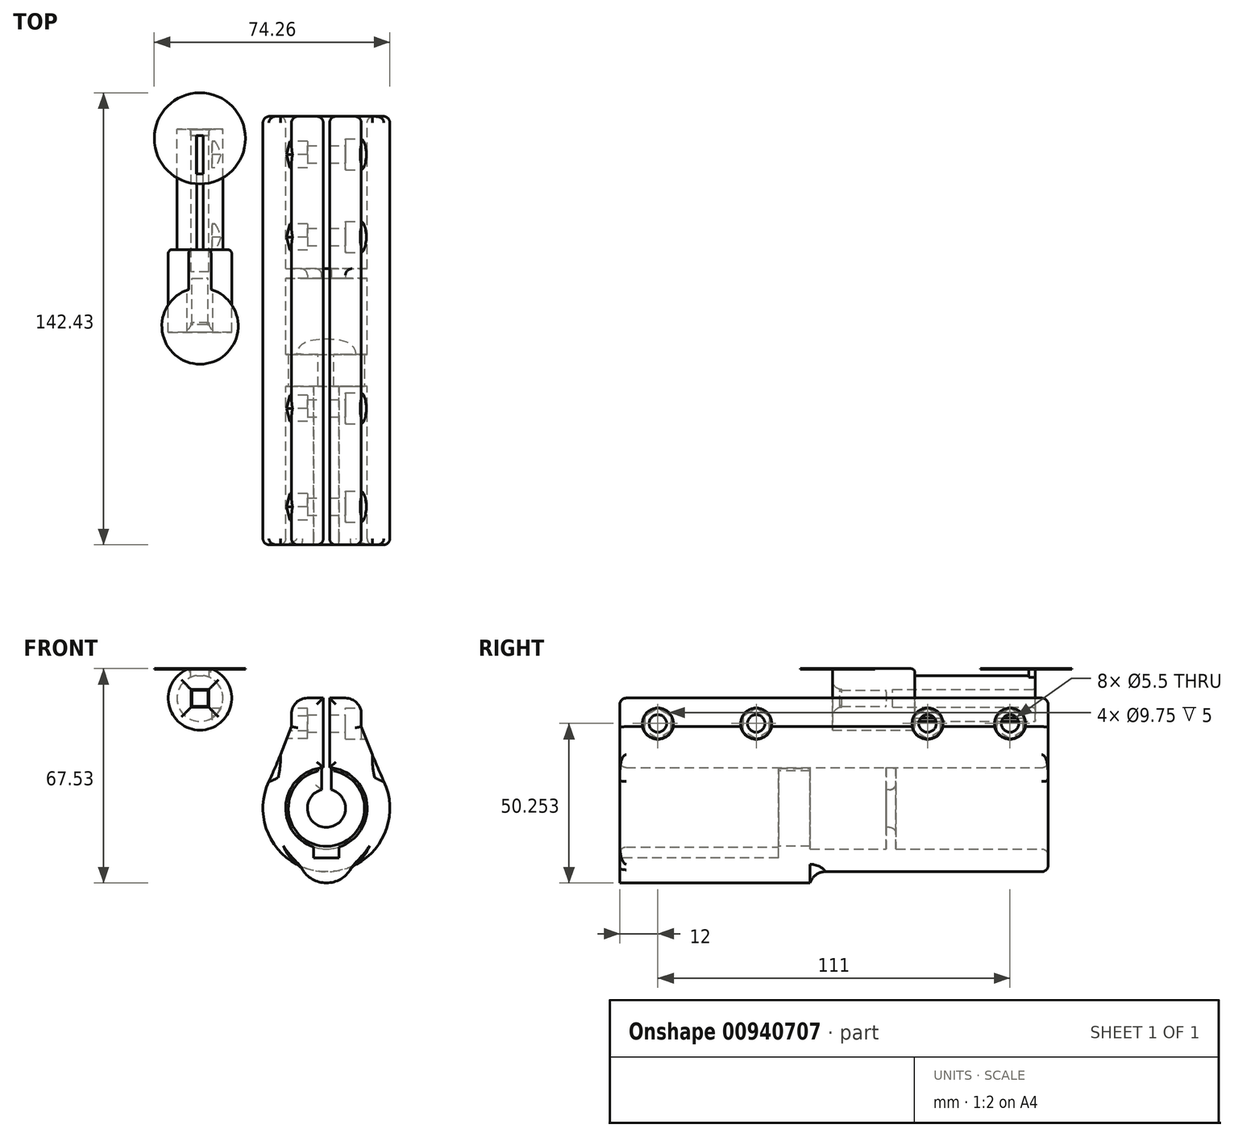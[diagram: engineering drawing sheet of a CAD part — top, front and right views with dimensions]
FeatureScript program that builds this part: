
annotation { "Feature Type Name" : "Feature", "Feature Type Description" : "" }
export const myFeature = defineFeature(function(context is Context, id is Id, definition is map)
    precondition{}
    {
        {
            var Q0;
            Q0=qCreatedBy(makeId("Front.planeOp"),FACE);
            var sketch = newSketch(context, id + "F0", { "sketchPlane" : qUnion([Q0])});
            skArc(sketch, "E0", {"start": v(-40.86, 41.8) * mm, "mid": v(-39.86, 27.36) * mm, "end": v(-38.86, 41.8) * mm});
            skLineSegment(sketch, "E1.bottom", {"start": v(-37.05, 31.8) * mm, "end": v(-42.67, 31.8) * mm});
            skLineSegment(sketch, "E1.top", {"start": v(-37.05, 37.42) * mm, "end": v(-42.67, 37.42) * mm});
            skLineSegment(sketch, "E1.left", {"start": v(-37.05, 31.8) * mm, "end": v(-37.05, 37.42) * mm});
            skLineSegment(sketch, "E1.right", {"start": v(-42.67, 31.8) * mm, "end": v(-42.67, 37.42) * mm});
            skLineSegment(sketch, "E2", {"start": v(-40.86, 41.8) * mm, "end": v(-38.86, 41.8) * mm});
            skArc(sketch, "E3", {"start": v(-43.36, 43.98) * mm, "mid": v(-39.86, 24.61) * mm, "end": v(-36.36, 43.98) * mm});
            skLineSegment(sketch, "E4", {"start": v(-43.36, 43.98) * mm, "end": v(-36.36, 43.98) * mm});
            skLineSegment(sketch, "E5.bottom", {"start": v(-37.76, 32.11) * mm, "end": v(-41.96, 32.11) * mm});
            skLineSegment(sketch, "E5.top", {"start": v(-37.76, 37.11) * mm, "end": v(-41.96, 37.11) * mm});
            skLineSegment(sketch, "E5.left", {"start": v(-37.36, 32.51) * mm, "end": v(-37.36, 36.71) * mm});
            skLineSegment(sketch, "E5.right", {"start": v(-42.36, 32.51) * mm, "end": v(-42.36, 36.71) * mm});
            skPoint(sketch, "E6.visualSharp", {"position": v(-42.36, 37.11) * mm});
            skArc(sketch, "E6.filletArc", {"start": v(-41.96, 37.11) * mm, "mid": v(-42.24, 37) * mm, "end": v(-42.36, 36.71) * mm});
            skPoint(sketch, "E7.visualSharp", {"position": v(-37.36, 37.11) * mm});
            skArc(sketch, "E7.filletArc", {"start": v(-37.36, 36.71) * mm, "mid": v(-37.48, 37) * mm, "end": v(-37.76, 37.11) * mm});
            skPoint(sketch, "E8.visualSharp", {"position": v(-37.36, 32.11) * mm});
            skArc(sketch, "E8.filletArc", {"start": v(-37.76, 32.11) * mm, "mid": v(-37.48, 32.23) * mm, "end": v(-37.36, 32.51) * mm});
            skPoint(sketch, "E9.visualSharp", {"position": v(-42.36, 32.11) * mm});
            skArc(sketch, "E9.filletArc", {"start": v(-42.36, 32.51) * mm, "mid": v(-42.24, 32.23) * mm, "end": v(-41.96, 32.11) * mm});
            skSolve(sketch);
        }
        {
            var Q0;
            Q0=makeQuery(id+"F0.imprint","IMPRINT",FACE,{"disambiguationData":[TD([[makeQuery(id+"F0.imprint","IMPRINT",EDGE,{"derivedFrom":sQuery(id+"F0.wireOp",EDGE,"E0")}),1.0]])]});
            extrude(context, id + "F1", {"entities" : qUnion([Q0]), "depth" : 18 * mm, "offsetDistance" : 25 * mm, "hasSecondDirection" : true, "secondDirectionOppositeDirection" : true, "secondDirectionDepth" : 46 * mm});
        }
        {
            var Q0;
            Q0=makeQuery(id+"F0.imprint","IMPRINT",FACE,{"disambiguationData":[TD([[makeQuery(id+"F0.imprint","IMPRINT",EDGE,{"derivedFrom":sQuery(id+"F0.wireOp",EDGE,"E1.bottom")}),-1.0]])]});
            var Q1;
            Q1=makeQuery(id+"F0.imprint","IMPRINT",FACE,{"disambiguationData":[TD([[makeQuery(id+"F0.imprint","IMPRINT",EDGE,{"derivedFrom":sQuery(id+"F0.wireOp",EDGE,"E5.bottom")}),-1.0]])]});
            extrude(context, id + "F2", {"entities" : qUnion([Q0, Q1]), "depth" : 1 * mm, "offsetDistance" : 25 * mm, "hasSecondDirection" : true, "secondDirectionOppositeDirection" : true, "secondDirectionDepth" : 1 * mm});
        }
        {
            var Q0;
            Q0=makeQuery(id+"F1.opExtrude","CAP_EDGE",EDGE,{"disambiguationData":[OSD([sQuery(id+"F0.wireOp",EDGE,"E1.left")])],"isStart":true});
            var Q1;
            Q1=makeQuery(id+"F1.opExtrude","CAP_EDGE",EDGE,{"disambiguationData":[OSD([sQuery(id+"F0.wireOp",EDGE,"E1.top")])],"isStart":true});
            var Q2;
            Q2=makeQuery(id+"F1.opExtrude","CAP_EDGE",EDGE,{"disambiguationData":[OSD([sQuery(id+"F0.wireOp",EDGE,"E1.right")])],"isStart":true});
            var Q3;
            Q3=makeQuery(id+"F1.opExtrude","CAP_EDGE",EDGE,{"disambiguationData":[OSD([sQuery(id+"F0.wireOp",EDGE,"E1.bottom")])],"isStart":true});
            fillet(context, id + "F3", {"entities" : qUnion([Q0, Q1, Q2, Q3]), "radius" : 1 * mm, "tangentPropagation" : true, "allowEdgeOverflow" : false});
        }
        {
            var Q0;
            Q0=qCreatedBy(makeId("Front.planeOp"),FACE);
            var sketch = newSketch(context, id + "F4", { "sketchPlane" : qUnion([Q0])});
            skLineSegment(sketch, "E10", {"start": v(0, -133.96) * mm, "end": v(0, 109.5) * mm, "construction": true});
            skArc(sketch, "E11", {"start": v(-16.99, 10.56) * mm, "mid": v(0, -20) * mm, "end": v(16.99, 10.56) * mm});
            skArc(sketch, "E12", {"start": v(-1, 12.81) * mm, "mid": v(0, -12.85) * mm, "end": v(1, 12.81) * mm});
            skLineSegment(sketch, "E13.bottom", {"start": v(-11, 34.7) * mm, "end": v(-1, 34.7) * mm});
            skLineSegment(sketch, "E13.left", {"start": v(-11, 34.7) * mm, "end": v(-11, 25.7) * mm});
            skLineSegment(sketch, "E13.right", {"start": v(11, 34.7) * mm, "end": v(11, 25.7) * mm});
            skPoint(sketch, "E13.middle", {"position": v(0, 35.28) * mm});
            skPoint(sketch, "E14.trimOffspring.end.orphan", {"position": v(-11, 35.86) * mm});
            skPoint(sketch, "E15.trimOffspring.end.orphan", {"position": v(11, 35.86) * mm});
            skLineSegment(sketch, "E16.left", {"start": v(-1, 34.7) * mm, "end": v(-1, 12.81) * mm});
            skLineSegment(sketch, "E16.right", {"start": v(1, 34.7) * mm, "end": v(1, 12.81) * mm});
            skPoint(sketch, "E16.middle", {"position": v(0, 52.57) * mm});
            skPoint(sketch, "E17.orphan", {"position": v(1, 29.17) * mm});
            skPoint(sketch, "E16.top.start.orphan", {"position": v(-1, 29.19) * mm});
            skLineSegment(sketch, "E18.trimOffspring", {"start": v(1, 34.7) * mm, "end": v(11, 34.7) * mm});
            skPoint(sketch, "E19.orphan", {"position": v(-1, 75.98) * mm});
            skPoint(sketch, "E20.orphan", {"position": v(1, 75.96) * mm});
            skLineSegment(sketch, "E21", {"start": v(11, 25.7) * mm, "end": v(16.99, 10.56) * mm});
            skLineSegment(sketch, "E22.MirrorCS", {"start": v(-11, 25.7) * mm, "end": v(-16.99, 10.56) * mm});
            skPoint(sketch, "E23.orphan", {"position": v(11, 16.7) * mm});
            skSolve(sketch);
        }
        {
            var Q0;
            Q0=makeQuery(id+"F4.imprint","IMPRINT",FACE,{"disambiguationData":[TD([[makeQuery(id+"F4.imprint","IMPRINT",EDGE,{"derivedFrom":sQuery(id+"F4.wireOp",EDGE,"E11")}),1.0]])]});
            extrude(context, id + "F5", {"entities" : qUnion([Q0]), "depth" : 85 * mm, "offsetDistance" : 25 * mm, "hasSecondDirection" : true, "secondDirectionOppositeDirection" : true, "secondDirectionDepth" : 50 * mm});
        }
        {
            var Q0;
            Q0=makeQuery(id+"F5.opExtrude","CAP_EDGE",EDGE,{"disambiguationData":[OSD([sQuery(id+"F4.wireOp",EDGE,"E12")])],"isStart":true});
            var Q1;
            Q1=makeQuery(id+"F5.opExtrude","CAP_EDGE",EDGE,{"disambiguationData":[OSD([sQuery(id+"F4.wireOp",EDGE,"E12")])],"isStart":false});
            var Q2;
            Q2=makeQuery(id+"F5.opExtrude","CAP_EDGE",EDGE,{"disambiguationData":[OSD([sQuery(id+"F4.wireOp",EDGE,"E11")])],"isStart":true});
            var Q3;
            Q3=makeQuery(id+"F5.opExtrude","CAP_FACE",FACE,{"disambiguationData":[OSD([sQuery(id+"F4.wireOp",EDGE,"E11"),sQuery(id+"F4.wireOp",EDGE,"E12"),sQuery(id+"F4.wireOp",EDGE,"E13.bottom"),sQuery(id+"F4.wireOp",EDGE,"E13.left"),sQuery(id+"F4.wireOp",EDGE,"E13.right"),sQuery(id+"F4.wireOp",EDGE,"E16.left"),sQuery(id+"F4.wireOp",EDGE,"E16.right"),sQuery(id+"F4.wireOp",EDGE,"E18.trimOffspring")])],"isStart":true});
            var Q4;
            Q4=makeQuery(id+"F5.opExtrude","CAP_FACE",FACE,{"disambiguationData":[OSD([sQuery(id+"F4.wireOp",EDGE,"E11"),sQuery(id+"F4.wireOp",EDGE,"E12"),sQuery(id+"F4.wireOp",EDGE,"E13.bottom"),sQuery(id+"F4.wireOp",EDGE,"E13.left"),sQuery(id+"F4.wireOp",EDGE,"E13.right"),sQuery(id+"F4.wireOp",EDGE,"E16.left"),sQuery(id+"F4.wireOp",EDGE,"E16.right"),sQuery(id+"F4.wireOp",EDGE,"E18.trimOffspring")])],"isStart":false});
            fillet(context, id + "F6", {"entities" : qUnion([Q0, Q1, Q2, Q3, Q4]), "radius" : 2 * mm, "tangentPropagation" : true, "allowEdgeOverflow" : false});
        }
        {
            var Q0;
            Q0=makeQuery(id+"F5.opExtrude","SWEPT_FACE",FACE,{"disambiguationData":[OSD([sQuery(id+"F4.wireOp",EDGE,"E13.right")])]});
            var sketch = newSketch(context, id + "F7", { "sketchPlane" : qUnion([Q0])});
            skLineSegment(sketch, "E24", {"start": v(-11, 26.7) * mm, "end": v(-81, 26.7) * mm, "construction": true});
            skPoint(sketch, "E25", {"position": v(38, 26.7) * mm});
            skPoint(sketch, "E26", {"position": v(12, 26.7) * mm});
            skPoint(sketch, "E27", {"position": v(-42, 26.7) * mm});
            skPoint(sketch, "E28", {"position": v(-73, 26.7) * mm});
            skSolve(sketch);
        }
        {
            var Q0;
            Q0=sQuery(id+"F7.wireOp",VERTEX,"E25");
            var Q1;
            Q1=sQuery(id+"F7.wireOp",VERTEX,"E26");
            var Q2;
            Q2=sQuery(id+"F7.wireOp",VERTEX,"E27");
            var Q3;
            Q3=sQuery(id+"F7.wireOp",VERTEX,"E28");
            var Q4;
            Q4=makeQuery(id+"F1.opExtrude","SWEPT_BODY",BODY,{"disambiguationData":[OSD([sQuery(id+"F0.wireOp",EDGE,"E0"),sQuery(id+"F0.wireOp",EDGE,"E1.bottom"),sQuery(id+"F0.wireOp",EDGE,"E1.top"),sQuery(id+"F0.wireOp",EDGE,"E1.left"),sQuery(id+"F0.wireOp",EDGE,"E1.right")])]});
            var Q5;
            Q5=makeQuery(id+"F5.opExtrude","SWEPT_BODY",BODY,{"disambiguationData":[OSD([sQuery(id+"F4.wireOp",EDGE,"E11"),sQuery(id+"F4.wireOp",EDGE,"E12"),sQuery(id+"F4.wireOp",EDGE,"E13.bottom"),sQuery(id+"F4.wireOp",EDGE,"E13.left"),sQuery(id+"F4.wireOp",EDGE,"E13.right"),sQuery(id+"F4.wireOp",EDGE,"E16.left"),sQuery(id+"F4.wireOp",EDGE,"E16.right"),sQuery(id+"F4.wireOp",EDGE,"E18.trimOffspring")])]});
            hole(context, id + "F8", {"style" : HoleStyle.C_BORE, "endStyle" : HoleEndStyle.BLIND, "standardTappedOrClearance" : lookupTablePath({ "fit" : "Normal", "standard" : "ISO", "size" : "M5", "type" : "Clearance" }), "standardBlindInLast" : lookupTablePath({ "fit" : "Normal", "standard" : "ISO", "engagement" : "75%", "pitch" : "0.8 mm", "size" : "M5", "type" : "Clearance & tapped" }), "holeDiameter" : 5.5 * mm, "cBoreDiameter" : 9.75 * mm, "cBoreDepth" : 5 * mm, "majorDiameter" : 5 * mm, "holeDepth" : 35 * mm, "isTappedThrough" : true, "tappedDepth" : 12 * mm, "tapClearance" : 3, "locations" : qUnion([Q0, Q1, Q2, Q3]), "scope" : qUnion([Q4, Q5])});
        }
        {
            var Q0;
            Q0=makeQuery(id+"F5.opExtrude","SWEPT_FACE",FACE,{"disambiguationData":[OSD([sQuery(id+"F4.wireOp",EDGE,"E13.left")])]});
            var sketch = newSketch(context, id + "F9", { "sketchPlane" : qUnion([Q0])});
            skPoint(sketch, "E29", {"position": v(73, 26.7) * mm});
            skPoint(sketch, "E30", {"position": v(42, 26.7) * mm});
            skPoint(sketch, "E31", {"position": v(-12, 26.7) * mm});
            skPoint(sketch, "E32", {"position": v(-38, 26.7) * mm});
            skCircle(sketch, "E33.cCircle", {"center": v(73, 26.7) * mm, "radius": 4.15 * mm, "construction": true});
            skLineSegment(sketch, "E33.0", {"start": v(77.15, 29.1) * mm, "end": v(77.15, 24.3) * mm});
            skLineSegment(sketch, "E33.1", {"start": v(77.15, 24.3) * mm, "end": v(73, 21.91) * mm});
            skLineSegment(sketch, "E33.2", {"start": v(73, 21.91) * mm, "end": v(68.85, 24.3) * mm});
            skLineSegment(sketch, "E33.3", {"start": v(68.85, 24.3) * mm, "end": v(68.85, 29.1) * mm});
            skLineSegment(sketch, "E33.4", {"start": v(68.85, 29.1) * mm, "end": v(73, 31.5) * mm});
            skLineSegment(sketch, "E33.5", {"start": v(73, 31.5) * mm, "end": v(77.15, 29.1) * mm});
            skPoint(sketch, "E33.0.midPoint", {"position": v(77.15, 26.7) * mm});
            skCircle(sketch, "E34.cCircle", {"center": v(42, 26.7) * mm, "radius": 4.15 * mm, "construction": true});
            skLineSegment(sketch, "E34.0", {"start": v(46.15, 29.1) * mm, "end": v(46.15, 24.3) * mm});
            skLineSegment(sketch, "E34.1", {"start": v(46.15, 24.3) * mm, "end": v(42, 21.91) * mm});
            skLineSegment(sketch, "E34.2", {"start": v(42, 21.91) * mm, "end": v(37.85, 24.3) * mm});
            skLineSegment(sketch, "E34.3", {"start": v(37.85, 24.3) * mm, "end": v(37.85, 29.1) * mm});
            skLineSegment(sketch, "E34.4", {"start": v(37.85, 29.1) * mm, "end": v(42, 31.5) * mm});
            skLineSegment(sketch, "E34.5", {"start": v(42, 31.5) * mm, "end": v(46.15, 29.1) * mm});
            skPoint(sketch, "E34.0.midPoint", {"position": v(46.15, 26.7) * mm});
            skCircle(sketch, "E35.cCircle", {"center": v(-12, 26.7) * mm, "radius": 4.15 * mm, "construction": true});
            skLineSegment(sketch, "E35.0", {"start": v(-7.85, 29.1) * mm, "end": v(-7.85, 24.3) * mm});
            skLineSegment(sketch, "E35.1", {"start": v(-7.85, 24.3) * mm, "end": v(-12, 21.91) * mm});
            skLineSegment(sketch, "E35.2", {"start": v(-12, 21.91) * mm, "end": v(-16.15, 24.3) * mm});
            skLineSegment(sketch, "E35.3", {"start": v(-16.15, 24.3) * mm, "end": v(-16.15, 29.1) * mm});
            skLineSegment(sketch, "E35.4", {"start": v(-16.15, 29.1) * mm, "end": v(-12, 31.5) * mm});
            skLineSegment(sketch, "E35.5", {"start": v(-12, 31.5) * mm, "end": v(-7.85, 29.1) * mm});
            skPoint(sketch, "E35.0.midPoint", {"position": v(-7.85, 26.7) * mm});
            skCircle(sketch, "E36.cCircle", {"center": v(-38, 26.7) * mm, "radius": 4.15 * mm, "construction": true});
            skLineSegment(sketch, "E36.0", {"start": v(-33.85, 29.1) * mm, "end": v(-33.85, 24.3) * mm});
            skLineSegment(sketch, "E36.1", {"start": v(-33.85, 24.3) * mm, "end": v(-38, 21.91) * mm});
            skLineSegment(sketch, "E36.2", {"start": v(-38, 21.91) * mm, "end": v(-42.15, 24.3) * mm});
            skLineSegment(sketch, "E36.3", {"start": v(-42.15, 24.3) * mm, "end": v(-42.15, 29.1) * mm});
            skLineSegment(sketch, "E36.4", {"start": v(-42.15, 29.1) * mm, "end": v(-38, 31.5) * mm});
            skLineSegment(sketch, "E36.5", {"start": v(-38, 31.5) * mm, "end": v(-33.85, 29.1) * mm});
            skPoint(sketch, "E36.0.midPoint", {"position": v(-33.85, 26.7) * mm});
            skSolve(sketch);
        }
        {
            var Q0;
            Q0=qCreatedBy(makeId("Front.planeOp"),FACE);
            var sketch = newSketch(context, id + "F10", { "sketchPlane" : qUnion([Q0])});
            skArc(sketch, "E37", {"start": v(-1.43, 5.83) * mm, "mid": v(-0.07, -6) * mm, "end": v(1.57, 5.8) * mm});
            skArc(sketch, "E38", {"start": v(-1.43, 14.93) * mm, "mid": v(-0.07, -15) * mm, "end": v(1.57, 14.92) * mm});
            skLineSegment(sketch, "E39", {"start": v(-1.43, 14.93) * mm, "end": v(-1.43, 5.83) * mm});
            skLineSegment(sketch, "E40", {"start": v(1.57, 14.92) * mm, "end": v(1.57, 5.8) * mm});
            skSolve(sketch);
        }
        {
            var Q0;
            Q0=makeQuery(id+"F9.imprint","IMPRINT",FACE,{"disambiguationData":[TD([[makeQuery(id+"F9.imprint","IMPRINT",EDGE,{"derivedFrom":sQuery(id+"F9.wireOp",EDGE,"E33.0")}),-1.0]])]});
            var Q1;
            Q1=makeQuery(id+"F9.imprint","IMPRINT",FACE,{"disambiguationData":[TD([[makeQuery(id+"F9.imprint","IMPRINT",EDGE,{"derivedFrom":sQuery(id+"F9.wireOp",EDGE,"E34.0")}),-1.0]])]});
            var Q2;
            Q2=makeQuery(id+"F9.imprint","IMPRINT",FACE,{"disambiguationData":[TD([[makeQuery(id+"F9.imprint","IMPRINT",EDGE,{"derivedFrom":sQuery(id+"F9.wireOp",EDGE,"E35.0")}),-1.0]])]});
            var Q3;
            Q3=makeQuery(id+"F9.imprint","IMPRINT",FACE,{"disambiguationData":[TD([[makeQuery(id+"F9.imprint","IMPRINT",EDGE,{"derivedFrom":sQuery(id+"F9.wireOp",EDGE,"E36.0")}),-1.0]])]});
            extrude(context, id + "F11", {"entities" : qUnion([Q0, Q1, Q2, Q3]), "operationType" : NewBodyOperationType.REMOVE, "oppositeDirection" : true, "depth" : 5 * mm, "offsetDistance" : 25 * mm, "hasSecondDirection" : true, "secondDirectionOppositeDirection" : false, "secondDirectionDepth" : 25 * mm});
        }
        {
            var Q0;
            Q0=makeQuery(id+"F10.imprint","IMPRINT",FACE,{"disambiguationData":[TD([[makeQuery(id+"F10.imprint","IMPRINT",EDGE,{"derivedFrom":sQuery(id+"F10.wireOp",EDGE,"E37")}),-1.0]])]});
            extrude(context, id + "F12", {"entities" : qUnion([Q0]), "operationType" : NewBodyOperationType.ADD, "oppositeDirection" : true, "depth" : 2 * mm, "offsetDistance" : 25 * mm, "hasSecondDirection" : true, "secondDirectionOppositeDirection" : false, "secondDirectionDepth" : 1 * mm});
        }
        {
            var Q0;
            Q0=makeQuery(id+"F5.opExtrude","CAP_FACE",FACE,{"disambiguationData":[OSD([sQuery(id+"F4.wireOp",EDGE,"E11"),sQuery(id+"F4.wireOp",EDGE,"E12"),sQuery(id+"F4.wireOp",EDGE,"E13.bottom"),sQuery(id+"F4.wireOp",EDGE,"E13.left"),sQuery(id+"F4.wireOp",EDGE,"E13.right"),sQuery(id+"F4.wireOp",EDGE,"E16.left"),sQuery(id+"F4.wireOp",EDGE,"E16.right"),sQuery(id+"F4.wireOp",EDGE,"E18.trimOffspring")])],"isStart":false});
            var sketch = newSketch(context, id + "F13", { "sketchPlane" : qUnion([Q0])});
            skArc(sketch, "E41", {"start": v(-2.6, 14.51) * mm, "mid": v(0.17, -14.75) * mm, "end": v(2.27, 14.57) * mm});
            skArc(sketch, "E42", {"start": v(-2.6, 11.71) * mm, "mid": v(0.17, -12) * mm, "end": v(2.27, 11.78) * mm});
            skLineSegment(sketch, "E43", {"start": v(2.27, 11.78) * mm, "end": v(2.27, 14.57) * mm});
            skLineSegment(sketch, "E44", {"start": v(-2.6, 11.71) * mm, "end": v(-2.6, 14.51) * mm});
            skSolve(sketch);
        }
        {
            var Q0;
            {var subQ0=sQuery(id+"F13.wireOp",EDGE,"E42");Q0=makeQuery(id+"F13.imprint","IMPRINT",FACE,{"disambiguationData":[TD([[makeQuery(id+"F13.imprint","IMPRINT",EDGE,{"derivedFrom":subQ0}),-1.0]])]});}
            extrude(context, id + "F14", {"entities" : qUnion([Q0]), "operationType" : NewBodyOperationType.ADD, "oppositeDirection" : true, "depth" : 60 * mm, "offsetDistance" : 25 * mm, "hasSecondDirection" : true, "secondDirectionOppositeDirection" : true, "secondDirectionDepth" : 50 * mm});
        }
        {
            var Q0;
            Q0=makeQuery(id+"F5.opExtrude","CAP_FACE",FACE,{"disambiguationData":[OSD([sQuery(id+"F4.wireOp",EDGE,"E11"),sQuery(id+"F4.wireOp",EDGE,"E12"),sQuery(id+"F4.wireOp",EDGE,"E13.bottom"),sQuery(id+"F4.wireOp",EDGE,"E13.left"),sQuery(id+"F4.wireOp",EDGE,"E13.right"),sQuery(id+"F4.wireOp",EDGE,"E16.left"),sQuery(id+"F4.wireOp",EDGE,"E16.right"),sQuery(id+"F4.wireOp",EDGE,"E18.trimOffspring")])],"isStart":false});
            var sketch = newSketch(context, id + "F15", { "sketchPlane" : qUnion([Q0])});
            skPoint(sketch, "E45.middle", {"position": v(0, -14.85) * mm});
            skLineSegment(sketch, "E46.bottom", {"start": v(4, -15.65) * mm, "end": v(-4, -15.65) * mm});
            skLineSegment(sketch, "E46.top", {"start": v(4, -12.05) * mm, "end": v(-4, -12.05) * mm});
            skLineSegment(sketch, "E46.left", {"start": v(4, -15.65) * mm, "end": v(4, -12.05) * mm});
            skLineSegment(sketch, "E46.right", {"start": v(-4, -15.65) * mm, "end": v(-4, -12.05) * mm});
            skPoint(sketch, "E46.middle", {"position": v(0, -13.85) * mm});
            skLineSegment(sketch, "E47", {"start": v(18.08, -15.7) * mm, "end": v(-26.62, -15.7) * mm, "construction": true});
            skArc(sketch, "E48", {"start": v(-8.8, -15.7) * mm, "mid": v(0, -23.55) * mm, "end": v(8.8, -15.7) * mm});
            skSolve(sketch);
        }
        {
            var Q0;
            {var subQ0=sQuery(id+"F15.wireOp",EDGE,"E46.top");Q0=makeQuery(id+"F15.imprint","IMPRINT",FACE,{"disambiguationData":[TD([[makeQuery(id+"F15.imprint","IMPRINT",EDGE,{"derivedFrom":subQ0}),1.0]])]});}
            var Q1;
            {var subQ0=sQuery(id+"F15.wireOp",EDGE,"E46.bottom");Q1=makeQuery(id+"F15.imprint","IMPRINT",FACE,{"disambiguationData":[TD([[makeQuery(id+"F15.imprint","IMPRINT",EDGE,{"derivedFrom":subQ0}),-1.0]])]});}
            extrude(context, id + "F16", {"entities" : qUnion([Q0, Q1]), "operationType" : NewBodyOperationType.REMOVE, "oppositeDirection" : true, "depth" : 50 * mm, "offsetDistance" : 25 * mm});
        }
        {
            var Q0;
            Q0=makeQuery(id+"F0.imprint","IMPRINT",FACE,{"disambiguationData":[TD([[makeQuery(id+"F0.imprint","IMPRINT",EDGE,{"derivedFrom":sQuery(id+"F0.wireOp",EDGE,"E0")}),-1.0]])]});
            extrude(context, id + "F17", {"entities" : qUnion([Q0]), "operationType" : NewBodyOperationType.ADD, "depth" : 18 * mm, "offsetDistance" : 25 * mm, "hasSecondDirection" : true, "secondDirectionOppositeDirection" : true, "secondDirectionDepth" : 8 * mm});
        }
        {
            var Q0;
            Q0=makeQuery(id+"F1.opExtrude","CAP_EDGE",EDGE,{"disambiguationData":[OSD([sQuery(id+"F0.wireOp",EDGE,"E1.top")])],"isStart":false});
            var Q1;
            Q1=makeQuery(id+"F1.opExtrude","CAP_EDGE",EDGE,{"disambiguationData":[OSD([sQuery(id+"F0.wireOp",EDGE,"E1.left")])],"isStart":false});
            var Q2;
            Q2=makeQuery(id+"F1.opExtrude","CAP_EDGE",EDGE,{"disambiguationData":[OSD([sQuery(id+"F0.wireOp",EDGE,"E1.bottom")])],"isStart":false});
            var Q3;
            Q3=makeQuery(id+"F1.opExtrude","CAP_EDGE",EDGE,{"disambiguationData":[OSD([sQuery(id+"F0.wireOp",EDGE,"E1.right")])],"isStart":false});
            fillet(context, id + "F18", {"entities" : qUnion([Q0, Q1, Q2, Q3]), "radius" : 3 * mm, "tangentPropagation" : true, "allowEdgeOverflow" : false});
        }
        {
            var Q0;
            Q0=makeQuery(id+"F17.opExtrude","CAP_EDGE",EDGE,{"disambiguationData":[OSD([sQuery(id+"F0.wireOp",EDGE,"E0")])],"isStart":true});
            var Q1;
            Q1=makeQuery(id+"F17.opExtrude","CAP_EDGE",EDGE,{"disambiguationData":[OSD([sQuery(id+"F0.wireOp",EDGE,"E2")])],"isStart":true});
            fillet(context, id + "F19", {"entities" : qUnion([Q0, Q1]), "radius" : 1.45 * mm, "tangentPropagation" : true, "allowEdgeOverflow" : false});
        }
        {
            var Q0;
            Q0=makeQuery(id+"F17.opExtrude","CAP_EDGE",EDGE,{"disambiguationData":[OSD([sQuery(id+"F0.wireOp",EDGE,"E3")])],"isStart":true});
            var Q1;
            Q1=makeQuery(id+"F17.opExtrude","CAP_EDGE",EDGE,{"disambiguationData":[OSD([sQuery(id+"F0.wireOp",EDGE,"E4")])],"isStart":true});
            fillet(context, id + "F20", {"entities" : qUnion([Q0, Q1]), "radius" : 1.2 * mm, "tangentPropagation" : true, "allowEdgeOverflow" : false});
        }
        {
            var Q0;
            Q0=makeQuery(id+"F5.opExtrude","SWEPT_EDGE",EDGE,{"disambiguationData":[OSD([sQuery(id+"F4.wireOp",EDGE,"E13.right"),sQuery(id+"F4.wireOp",EDGE,"E18.trimOffspring")])]});
            var Q1;
            Q1=makeQuery(id+"F5.opExtrude","SWEPT_EDGE",EDGE,{"disambiguationData":[OSD([sQuery(id+"F4.wireOp",EDGE,"E13.bottom"),sQuery(id+"F4.wireOp",EDGE,"E13.left")])]});
            fillet(context, id + "F21", {"entities" : qUnion([Q0, Q1]), "radius" : 5 * mm, "tangentPropagation" : true, "allowEdgeOverflow" : false});
        }
        {
            var Q0;
            Q0=makeQuery(id+"F12.opExtrude","CAP_EDGE",EDGE,{"disambiguationData":[OSD([sQuery(id+"F10.wireOp",EDGE,"E37")])],"isStart":false});
            var Q1;
            Q1=makeQuery(id+"F12.opExtrude","CAP_EDGE",EDGE,{"disambiguationData":[OSD([sQuery(id+"F10.wireOp",EDGE,"E39")])],"isStart":false});
            fillet(context, id + "F22", {"entities" : qUnion([Q0, Q1]), "radius" : 2 * mm, "tangentPropagation" : true, "allowEdgeOverflow" : false});
        }
        {
            var Q0;
            {var subQ0=sQuery(id+"F15.wireOp",EDGE,"E48");Q0=makeQuery(id+"F15.imprint","IMPRINT",FACE,{"disambiguationData":[TD([[makeQuery(id+"F15.imprint","IMPRINT",EDGE,{"derivedFrom":subQ0}),1.0]])]});}
            extrude(context, id + "F23", {"entities" : qUnion([Q0]), "operationType" : NewBodyOperationType.ADD, "oppositeDirection" : true, "depth" : 60 * mm, "offsetDistance" : 25 * mm});
        }
        {
            var Q0;
            Q0=makeQuery(id+"F23.boolean.opBoolean","INTERSECT",EDGE,{"disambiguationData":[OD(0.0)],"derivedFrom":[makeQuery(id+"F5.opExtrude","SWEPT_FACE",FACE,{"disambiguationData":[OSD([sQuery(id+"F4.wireOp",EDGE,"E11")])]}),makeQuery(id+"F23.opExtrude","SWEPT_FACE",FACE,{"disambiguationData":[OSD([sQuery(id+"F15.wireOp",EDGE,"E48")])]})]});
            var Q1;
            Q1=makeQuery(id+"F23.boolean.opBoolean","INTERSECT",EDGE,{"disambiguationData":[OD(1.0)],"derivedFrom":[makeQuery(id+"F5.opExtrude","SWEPT_FACE",FACE,{"disambiguationData":[OSD([sQuery(id+"F4.wireOp",EDGE,"E11")])]}),makeQuery(id+"F23.opExtrude","SWEPT_FACE",FACE,{"disambiguationData":[OSD([sQuery(id+"F15.wireOp",EDGE,"E48")])]})]});
            fillet(context, id + "F24", {"entities" : qUnion([Q0, Q1]), "radius" : 5 * mm, "tangentPropagation" : true, "allowEdgeOverflow" : false});
        }
        {
            var Q0;
            {var subQ0=sQuery(id+"F4.wireOp",EDGE,"E11");Q0=makeQuery(id+"F23.boolean.opBoolean","INTERSECT",EDGE,{"derivedFrom":[makeQuery(id+"F5.opExtrude","SWEPT_FACE",FACE,{"disambiguationData":[OSD([subQ0])]}),makeQuery(id+"F23.opExtrude","CAP_FACE",FACE,{"disambiguationData":[OSD([subQ0,sQuery(id+"F4.wireOp",EDGE,"E12"),sQuery(id+"F4.wireOp",EDGE,"E13.bottom"),sQuery(id+"F4.wireOp",EDGE,"E13.left"),sQuery(id+"F4.wireOp",EDGE,"E13.right"),sQuery(id+"F4.wireOp",EDGE,"E16.left"),sQuery(id+"F4.wireOp",EDGE,"E16.right"),sQuery(id+"F4.wireOp",EDGE,"E18.trimOffspring"),sQuery(id+"F15.wireOp",EDGE,"E48")])],"isStart":false})]});}
            fillet(context, id + "F25", {"entities" : qUnion([Q0]), "radius" : 5 * mm, "tangentPropagation" : true, "allowEdgeOverflow" : false});
        }
        {
            var Q0;
            Q0=sQuery(id+"F7.wireOp",VERTEX,"E25");
            var Q1;
            Q1=sQuery(id+"F7.wireOp",VERTEX,"E26");
            var Q2;
            Q2=sQuery(id+"F7.wireOp",VERTEX,"E27");
            var Q3;
            Q3=sQuery(id+"F7.wireOp",VERTEX,"E28");
            var Q4;
            Q4=makeQuery(id+"F5.opExtrude","SWEPT_BODY",BODY,{"disambiguationData":[OSD([sQuery(id+"F4.wireOp",EDGE,"E11"),sQuery(id+"F4.wireOp",EDGE,"E12"),sQuery(id+"F4.wireOp",EDGE,"E13.bottom"),sQuery(id+"F4.wireOp",EDGE,"E13.left"),sQuery(id+"F4.wireOp",EDGE,"E13.right"),sQuery(id+"F4.wireOp",EDGE,"E16.left"),sQuery(id+"F4.wireOp",EDGE,"E16.right"),sQuery(id+"F4.wireOp",EDGE,"E18.trimOffspring"),sQuery(id+"F4.wireOp",EDGE,"E21"),sQuery(id+"F4.wireOp",EDGE,"E22.MirrorCS")])]});
            hole(context, id + "F26", {"style" : HoleStyle.SIMPLE, "endStyle" : HoleEndStyle.BLIND, "oppositeDirection" : true, "holeDiameter" : 10 * mm, "majorDiameter" : 5 * mm, "holeDepth" : 35 * mm, "isTappedThrough" : true, "tappedDepth" : 12 * mm, "tapClearance" : 3, "locations" : qUnion([Q0, Q1, Q2, Q3]), "scope" : qUnion([Q4])});
        }
        {
            var Q0;
            Q0=makeQuery(id+"F5.opExtrude","SWEPT_EDGE",EDGE,{"disambiguationData":[OSD([sQuery(id+"F4.wireOp",EDGE,"E11"),sQuery(id+"F4.wireOp",EDGE,"E21")])]});
            var Q1;
            Q1=makeQuery(id+"F5.opExtrude","SWEPT_EDGE",EDGE,{"disambiguationData":[OSD([sQuery(id+"F4.wireOp",EDGE,"E11"),sQuery(id+"F4.wireOp",EDGE,"E22.MirrorCS")])]});
            fillet(context, id + "F27", {"entities" : qUnion([Q0, Q1]), "radius" : 148.3 * mm, "tangentPropagation" : true, "allowEdgeOverflow" : false});
        }
        {
            var Q0;
            Q0=makeQuery(id+"F17.opExtrude","SWEPT_FACE",FACE,{"disambiguationData":[OSD([sQuery(id+"F0.wireOp",EDGE,"E4")])]});
            var sketch = newSketch(context, id + "F28", { "sketchPlane" : qUnion([Q0])});
            skLineSegment(sketch, "E49", {"start": v(-39.9, 0) * mm, "end": v(-39.9, 61.08) * mm, "construction": true});
            skCircle(sketch, "E50", {"center": v(-39.9, 43.07) * mm, "radius": 14.36 * mm});
            skLineSegment(sketch, "E51.bottom", {"start": v(-42.78, 45.88) * mm, "end": v(-36.87, 45.88) * mm});
            skLineSegment(sketch, "E51.top", {"start": v(-42.78, 43.94) * mm, "end": v(-36.87, 43.94) * mm});
            skLineSegment(sketch, "E51.left", {"start": v(-42.78, 45.88) * mm, "end": v(-42.78, 43.94) * mm});
            skLineSegment(sketch, "E51.right", {"start": v(-36.87, 45.88) * mm, "end": v(-36.87, 43.94) * mm});
            skLineSegment(sketch, "E52.bottom", {"start": v(-40.97, 43.94) * mm, "end": v(-38.89, 43.94) * mm});
            skLineSegment(sketch, "E52.top", {"start": v(-40.97, 31.9) * mm, "end": v(-38.89, 31.9) * mm});
            skLineSegment(sketch, "E52.left", {"start": v(-40.97, 43.94) * mm, "end": v(-40.97, 31.9) * mm});
            skLineSegment(sketch, "E52.right", {"start": v(-38.89, 43.94) * mm, "end": v(-38.89, 31.9) * mm});
            skCircle(sketch, "E53", {"center": v(-39.84, -16.04) * mm, "radius": 12.02 * mm});
            skSolve(sketch);
        }
        {
            var Q0;
            Q0=makeQuery(id+"F28.imprint","IMPRINT",FACE,{"disambiguationData":[TD([[makeQuery(id+"F28.imprint","IMPRINT",EDGE,{"derivedFrom":sQuery(id+"F28.wireOp",EDGE,"E52.bottom")}),-1.0]])]});
            var Q1;
            Q1=makeQuery(id+"F28.imprint","IMPRINT",FACE,{"disambiguationData":[TD([[makeQuery(id+"F28.imprint","IMPRINT",EDGE,{"derivedFrom":sQuery(id+"F28.wireOp",EDGE,"E50")}),1.0]])]});
            var Q2;
            Q2=makeQuery(id+"F28.imprint","IMPRINT",FACE,{"disambiguationData":[TD([[makeQuery(id+"F28.imprint","IMPRINT",EDGE,{"derivedFrom":sQuery(id+"F28.wireOp",EDGE,"E51.bottom")}),-1.0]])]});
            extrude(context, id + "F29", {"entities" : qUnion([Q0, Q1, Q2]), "oppositeDirection" : true, "depth" : 0.22 * mm, "offsetDistance" : 25 * mm});
        }
        {
            var Q0;
            Q0=makeQuery(id+"F28.imprint","IMPRINT",FACE,{"disambiguationData":[TD([[makeQuery(id+"F28.imprint","IMPRINT",EDGE,{"derivedFrom":sQuery(id+"F28.wireOp",EDGE,"E51.bottom")}),-1.0]])]});
            var Q1;
            Q1=makeQuery(id+"F28.imprint","IMPRINT",FACE,{"disambiguationData":[TD([[makeQuery(id+"F28.imprint","IMPRINT",EDGE,{"derivedFrom":sQuery(id+"F28.wireOp",EDGE,"E52.bottom")}),-1.0]])]});
            extrude(context, id + "F30", {"entities" : qUnion([Q0, Q1]), "operationType" : NewBodyOperationType.ADD, "oppositeDirection" : true, "depth" : 2.9 * mm, "offsetDistance" : 25 * mm});
        }
        {
            var Q0;
            {var subQ1=sQuery(id+"F0.wireOp",EDGE,"E4");var subQ7=makeQuery(id+"F17.opExtrude","CAP_EDGE",EDGE,{"disambiguationData":[OSD([subQ1])],"isStart":false});Q0=makeQuery(id+"F28.imprint","IMPRINT",FACE,{"disambiguationData":[TD([[makeQuery(id+"F28.imprint","IMPRINT",EDGE,{"derivedFrom":subQ7}),1.0]])]});}
            var Q1;
            {var subQ1=sQuery(id+"F0.wireOp",EDGE,"E4");var subQ7=makeQuery(id+"F17.opExtrude","CAP_EDGE",EDGE,{"disambiguationData":[OSD([subQ1])],"isStart":false});Q1=makeQuery(id+"F28.imprint","IMPRINT",FACE,{"disambiguationData":[TD([[makeQuery(id+"F28.imprint","IMPRINT",EDGE,{"derivedFrom":subQ7}),-1.0]])]});}
            extrude(context, id + "F31", {"entities" : qUnion([Q0, Q1]), "operationType" : NewBodyOperationType.ADD, "oppositeDirection" : true, "depth" : 0.2 * mm, "offsetDistance" : 25 * mm});
        }
        {
            var Q0;
            Q0=makeQuery(id+"F0.imprint","IMPRINT",FACE,{"disambiguationData":[TD([[makeQuery(id+"F0.imprint","IMPRINT",EDGE,{"derivedFrom":sQuery(id+"F0.wireOp",EDGE,"E1.bottom")}),-1.0]])]});
            extrude(context, id + "F32", {"entities" : qUnion([Q0]), "operationType" : NewBodyOperationType.ADD, "depth" : 15.66 * mm, "offsetDistance" : 25 * mm});
        }
        {
            var Q0;
            Q0=makeQuery(id+"F32.opExtrude","CAP_EDGE",EDGE,{"disambiguationData":[OSD([sQuery(id+"F0.wireOp",EDGE,"E5.right")])],"isStart":false});
            fillet(context, id + "F33", {"entities" : qUnion([Q0]), "radius" : 0.4 * mm, "tangentPropagation" : true, "allowEdgeOverflow" : false});
        }
    });
